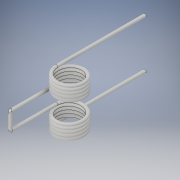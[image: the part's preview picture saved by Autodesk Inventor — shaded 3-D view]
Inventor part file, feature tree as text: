
AUTODESK INVENTOR PART (.ipt)
format: ipt  version: 2018 (Build 220112000, 112)  size: 375,808 bytes
history: native  units: in
note: dims shown in document units (in); Inventor stores cm internally (conversion verified against a paired STEP export)
features: sketch x9, extrude x8, projected_geometry x4, plane x2, helix x1, mirror x1
ambient origin geometry x8: Origin, YZ Plane, XZ Plane, XY Plane, X Axis, Y Axis, Z Axis, Center Point
bodies: Solid1 (feature_tree)
feature tree (25):
  helix  "Coil1"  [1 undecoded]
  extrude  "Extrusion1"  Depth=1.3in TaperAngle=0.0deg
  extrude  "Extrusion2"  Depth=0.0225in
  extrude  "Extrusion3"  Depth=0.7in TaperAngle=0.0deg
  extrude  "Extrusion4"  Depth=0.7in TaperAngle=0.0deg
  extrude  "Extrusion5"  Depth=0.045in
  plane  "Work Plane1"
  extrude  "Extrusion6"  Depth=0.7in TaperAngle=0.0deg
  extrude  "Extrusion7"  [1 undecoded]
  mirror  "Mirror1"
  extrude  "Extrusion8"  [1 undecoded]
  sketch  "Sketch1"  dims[d1=0.215in]
  sketch  "Sketch2"  dims[d2=0.23in d3=0.23in d4=1.9685in d5=0.0in d6=90.0deg d7=90.0deg d8=0.0in d9=0.0in d10=1.3in d11=0.0in]
  projected_geometry  "Projected Loop1"
  sketch  "Sketch3"  dims[d12=0.7in d13=0.0in d14=0.0225in]
  sketch  "Sketch4"  dims[d15=0.4in d16=0.0in d17=0.7in d18=0.0in]
  projected_geometry  "Projected Loop2"
  sketch  "Sketch5"  dims[d19=0.1475in d20=0.7in d21=0.35in d22=0.0in d23=0.0in]
  projected_geometry  "Projected Loop3"
  sketch  "Sketch6"  dims[d24=0.0in d25=0.045in]
  sketch  "Sketch7"  dims[d26=0.7in d27=0.0in d28=0.7in d29=0.0in]
  sketch  "Sketch8"  dims[d30=0.1in d31=0.0in]
  plane  "Work Plane2"
  sketch  "Sketch9"
  projected_geometry  "Projected Loop4"
note: 3 required parameter values undecoded (feature->parameter linkage not recoverable at this tier; creation-order binding heuristic only, values carry confidence <= 0.55)
